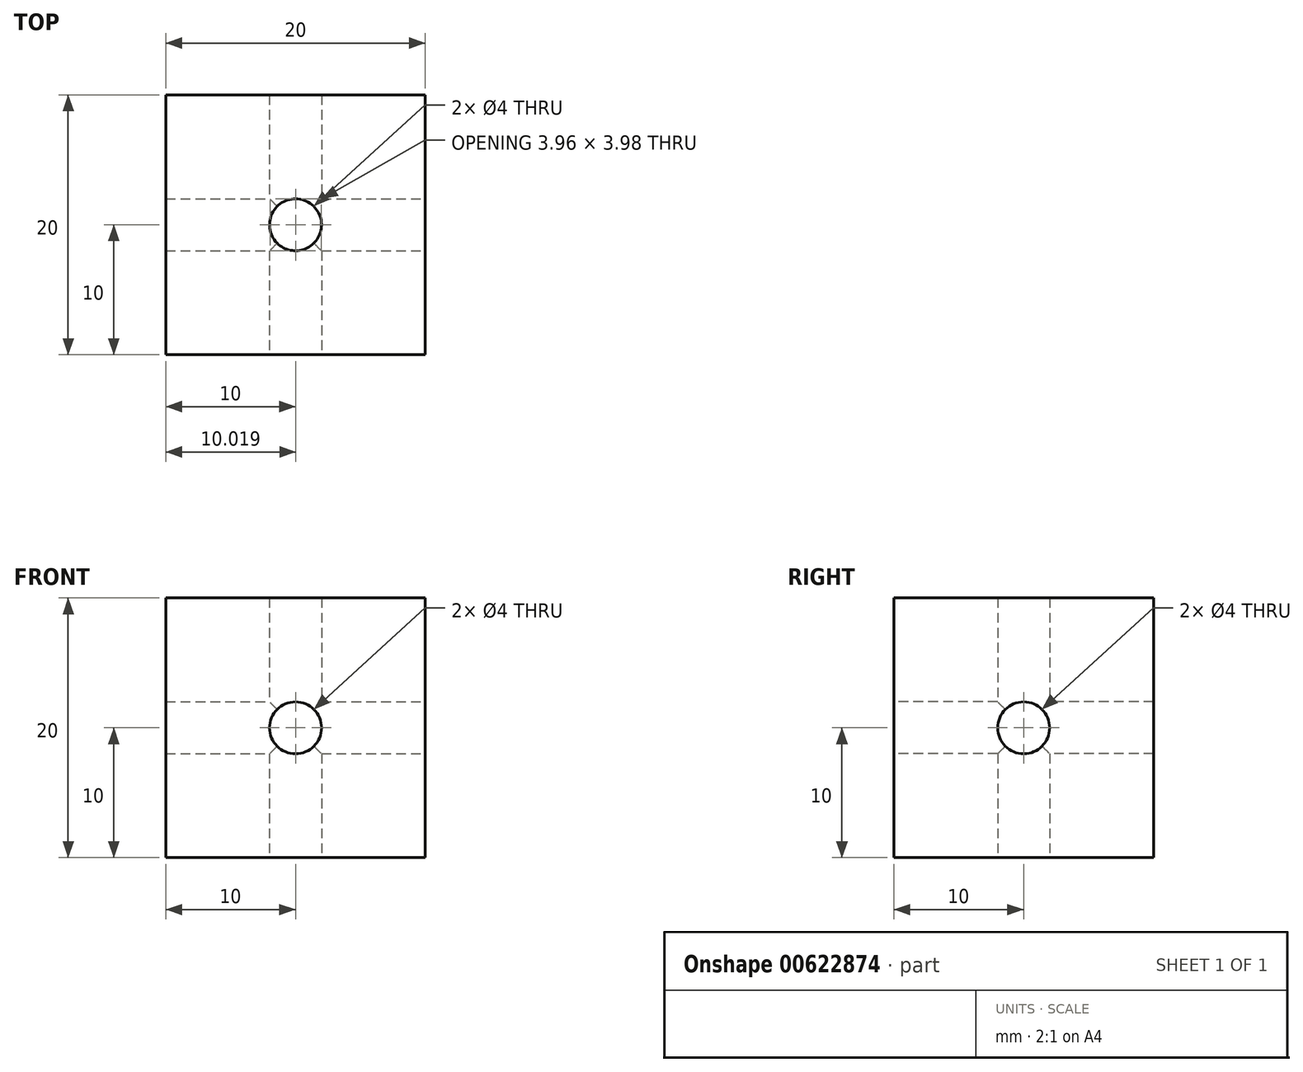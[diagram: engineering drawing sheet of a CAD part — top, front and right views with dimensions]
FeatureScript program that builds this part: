
annotation { "Feature Type Name" : "Feature", "Feature Type Description" : "" }
export const myFeature = defineFeature(function(context is Context, id is Id, definition is map)
    precondition{}
    {
        {
            var Q0;
            Q0=qCreatedBy(makeId("Top.planeOp"),FACE);
            var sketch = newSketch(context, id + "F0", { "sketchPlane" : qUnion([Q0])});
            skLineSegment(sketch, "E0.bottom", {"start": v(0, 0) * mm, "end": v(20, 0) * mm});
            skLineSegment(sketch, "E0.top", {"start": v(0, -20) * mm, "end": v(20, -20) * mm});
            skLineSegment(sketch, "E0.left", {"start": v(0, 0) * mm, "end": v(0, -20) * mm});
            skLineSegment(sketch, "E0.right", {"start": v(20, 0) * mm, "end": v(20, -20) * mm});
            skCircle(sketch, "E1", {"center": v(10, -10) * mm, "radius": 2 * mm});
            skPoint(sketch, "E1.centerSnap0", {"position": v(0, -10) * mm});
            skPoint(sketch, "E1.centerSnap1", {"position": v(10, 0) * mm});
            skSolve(sketch);
        }
        {
            var Q0;
            Q0=makeQuery(id+"F0.imprint","IMPRINT",FACE,{"disambiguationData":[TD([[makeQuery(id+"F0.imprint","IMPRINT",EDGE,{"derivedFrom":sQuery(id+"F0.wireOp",EDGE,"E0.bottom")}),-1.0]])]});
            extrude(context, id + "F1", {"entities" : qUnion([Q0]), "depth" : 20 * mm, "offsetDistance" : 25 * mm});
        }
        {
            var Q0;
            Q0=makeQuery(id+"F1.opExtrude","SWEPT_FACE",FACE,{"disambiguationData":[OSD([sQuery(id+"F0.wireOp",EDGE,"E0.right")])]});
            var sketch = newSketch(context, id + "F2", { "sketchPlane" : qUnion([Q0])});
            skCircle(sketch, "E2", {"center": v(-10, 10) * mm, "radius": 2 * mm});
            skPoint(sketch, "E2.centerSnap0", {"position": v(-10, 20) * mm});
            skPoint(sketch, "E2.centerSnap1", {"position": v(0, 10) * mm});
            skSolve(sketch);
        }
        {
            var Q0;
            Q0=makeQuery(id+"F2.imprint","IMPRINT",FACE,{"disambiguationData":[TD([[makeQuery(id+"F2.imprint","IMPRINT",EDGE,{"derivedFrom":sQuery(id+"F2.wireOp",EDGE,"E2")}),1.0]])]});
            extrude(context, id + "F3", {"entities" : qUnion([Q0]), "operationType" : NewBodyOperationType.REMOVE, "endBound" : BoundingType.THROUGH_ALL, "oppositeDirection" : true, "depth" : 25 * mm, "offsetDistance" : 25 * mm});
        }
        {
            var Q0;
            Q0=makeQuery(id+"F1.opExtrude","SWEPT_FACE",FACE,{"disambiguationData":[OSD([sQuery(id+"F0.wireOp",EDGE,"E0.top")])]});
            var sketch = newSketch(context, id + "F4", { "sketchPlane" : qUnion([Q0])});
            skCircle(sketch, "E3", {"center": v(10, 10) * mm, "radius": 2 * mm});
            skPoint(sketch, "E3.centerSnap0", {"position": v(0, 10) * mm});
            skPoint(sketch, "E3.centerSnap1", {"position": v(10, 20) * mm});
            skSolve(sketch);
        }
        {
            var Q0;
            Q0=makeQuery(id+"F4.imprint","IMPRINT",FACE,{"disambiguationData":[TD([[makeQuery(id+"F4.imprint","IMPRINT",EDGE,{"derivedFrom":sQuery(id+"F4.wireOp",EDGE,"E3")}),1.0]])]});
            extrude(context, id + "F5", {"entities" : qUnion([Q0]), "operationType" : NewBodyOperationType.REMOVE, "endBound" : BoundingType.THROUGH_ALL, "oppositeDirection" : true, "depth" : 25 * mm, "offsetDistance" : 25 * mm});
        }
    });
